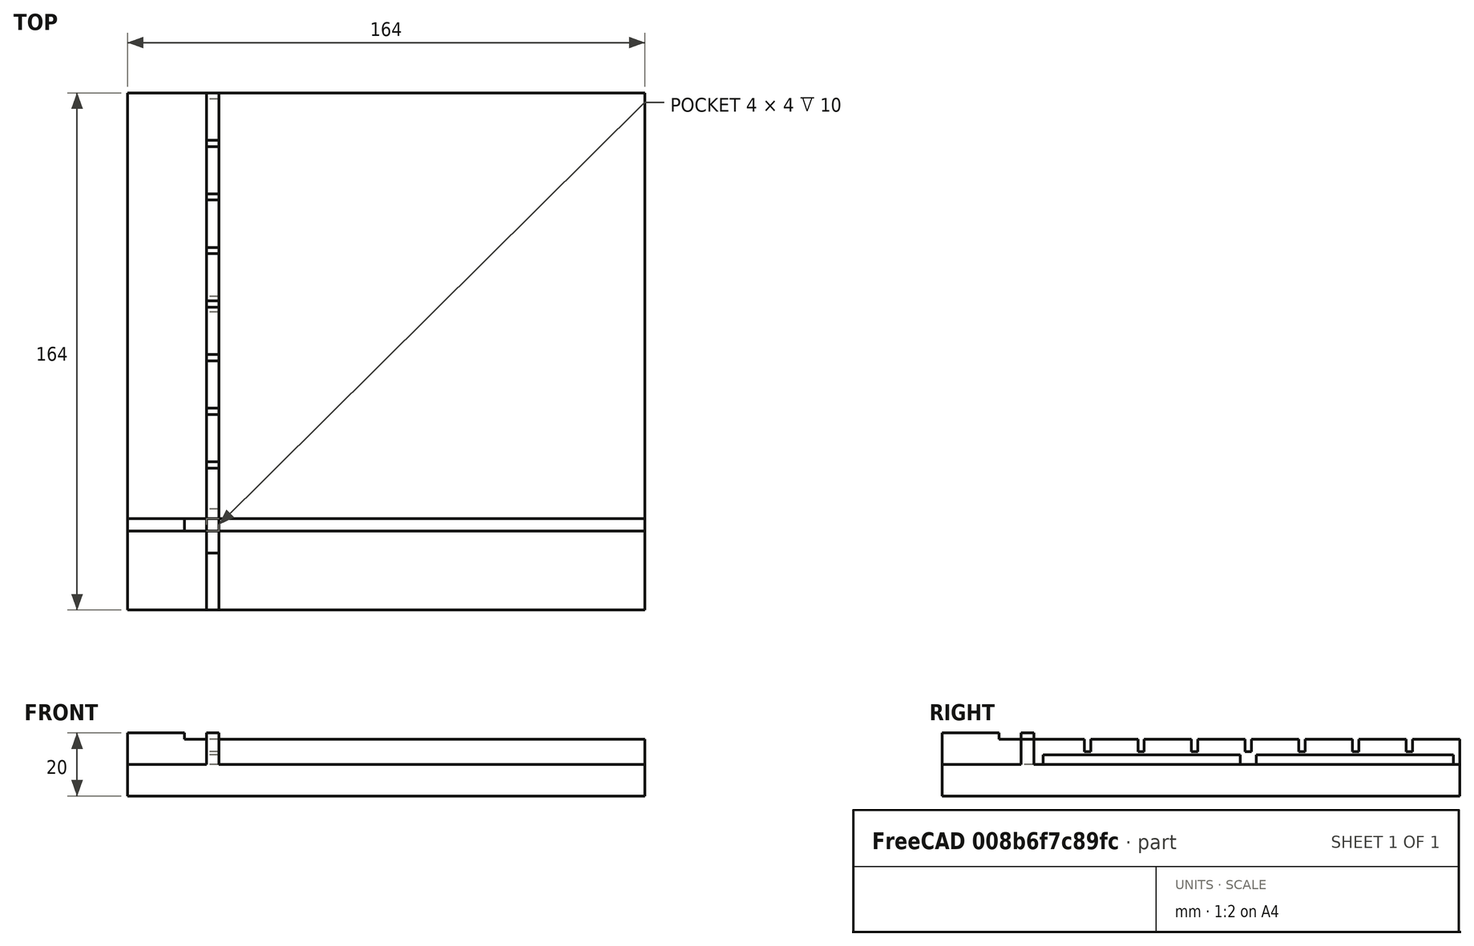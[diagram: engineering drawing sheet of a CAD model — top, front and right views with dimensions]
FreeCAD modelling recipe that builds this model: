
FCSTD DOCUMENT  (FreeCAD 2024.207R38947 (Git))
Label: frame_plate_left_bottom_debugging
License: All rights reserved
LicenseURL: http://en.wikipedia.org/wiki/All_rights_reserved
objects: Sketcher::SketchObject×7, PartDesign::Pocket×4, PartDesign::Pad×2, PartDesign::LinearPattern×1, PartDesign::Body×1
note: 36 computed .brp shape members not serialized (recipe doc carries the construction recipe); baked Part::Feature solids carry a one-line shape summary decoded from their .brp

FEATURE [Sketcher::SketchObject] Sketch  label="LB-plate"
  ArcFitTolerance = 0
  AttachmentSupport = -> [XY_Plane]
  ExternalBSplineMaxDegree = 0
  ExternalBSplineTolerance = 0
  FullyConstrained = true
  InternalTolerance = 1e-06
  InvalidShape = false
  MakeInternals = false
  MapMode = 5
  Support = -> [XY_Plane]
  TreeRank = 0
  ValidateShape = false
  sketch-geometry (4):
    g0: LineSegment StartX=-82 StartY=82 StartZ=0 EndX=82 EndY=82 EndZ=0
    g1: LineSegment StartX=82 StartY=82 StartZ=0 EndX=82 EndY=-82 EndZ=0
    g2: LineSegment StartX=82 StartY=-82 StartZ=0 EndX=-82 EndY=-82 EndZ=0
    g3: LineSegment StartX=-82 StartY=-82 StartZ=0 EndX=-82 EndY=82 EndZ=0
  constraints (10):
    c: Coincident(g0,g1)
    c: Coincident(g1,g2)
    c: Coincident(g2,g3)
    c: Coincident(g3,g0)
    c: Horizontal(g2)
    c: Vertical(g3)
    c: DistanceX(g2,g1) = 164
    c: DistanceY(g2,g0) = 164
    c: Symmetric(g1,g0,g-1)
    c: Symmetric(g0,g0,g-2)
FEATURE [PartDesign::Pad] Pad
  AddSubType = 0
  AutoTaperInnerAngle = true
  CheckUpToFaceLimits = true
  ClaimChildren = false
  Direction = (0,0,1)
  Fit = 0
  FitJoin = 0
  InnerFit = 0
  InnerFitJoin = 0
  InvalidShape = false
  Length = 10
  Length2 = 10
  NewSolid = false
  Profile = -> Sketch
  ReferenceAxis = -> Sketch [N_Axis]
  Suppress = false
  TaperInnerAngle = 0
  TaperInnerAngleRev = 0
  TreeRank = 0
  Type = 0
  ValidateShape = true
  _ProfileBasedVersion = 0
FEATURE [Sketcher::SketchObject] Sketch001  label="LB-bounds"
  ArcFitTolerance = 0
  AttachmentSupport = -> [Pad]
  ExternalBSplineMaxDegree = 0
  ExternalBSplineTolerance = 0
  FullyConstrained = true
  InternalTolerance = 1e-06
  InvalidShape = false
  MakeInternals = false
  MapMode = 5
  Placement = pos=(0,0,10) rot=(0,0,1;0rad)
  Support = -> [Pad]
  TreeRank = 0
  ValidateShape = false
  sketch-geometry (8):
    g0: LineSegment StartX=-82 StartY=-53 StartZ=0 EndX=82 EndY=-53 EndZ=0
    g1: LineSegment StartX=82 StartY=-53 StartZ=0 EndX=82 EndY=-57 EndZ=0
    g2: LineSegment StartX=82 StartY=-57 StartZ=0 EndX=-82 EndY=-57 EndZ=0
    g3: LineSegment StartX=-82 StartY=-57 StartZ=0 EndX=-82 EndY=-53 EndZ=0
    g4: LineSegment StartX=-53 StartY=82 StartZ=0 EndX=-57 EndY=82 EndZ=0
    g5: LineSegment StartX=-57 StartY=82 StartZ=0 EndX=-57 EndY=-82 EndZ=0
    g6: LineSegment StartX=-57 StartY=-82 StartZ=0 EndX=-53 EndY=-82 EndZ=0
    g7: LineSegment StartX=-53 StartY=-82 StartZ=0 EndX=-53 EndY=82 EndZ=0
  constraints (24):
    c: Coincident(g0,g1)
    c: Coincident(g1,g2)
    c: Coincident(g2,g3)
    c: Coincident(g3,g0)
    c: Horizontal(g0)
    c: Horizontal(g2)
    c: Vertical(g1)
    c: Vertical(g3)
    c: DistanceY(g2,g0) = 4
    c: Coincident(g4,g5)
    c: Coincident(g5,g6)
    c: Coincident(g6,g7)
    c: Coincident(g7,g4)
    c: Horizontal(g4)
    c: Horizontal(g6)
    c: Vertical(g5)
    c: Vertical(g7)
    c: DistanceX(g5,g6) = 4
    c: DistanceX(g2,g6) = 29
    c: DistanceY(g5,g0) = 29
    c: DistanceY(g0,g-1) = 53
    c: DistanceX(g6,g-1) = 53
    c: DistanceX(g2,g1) = 164
    c: DistanceY(g5,g4) = 164
FEATURE [PartDesign::Pad] Pad001
  AddSubType = 0
  AutoTaperInnerAngle = true
  BaseFeature = -> Pad
  CheckUpToFaceLimits = true
  ClaimChildren = false
  Direction = (0,0,1)
  Fit = 0
  FitJoin = 0
  InnerFit = 0
  InnerFitJoin = 0
  InvalidShape = false
  Length = 10
  Length2 = 10
  NewSolid = false
  Profile = -> Sketch001
  ReferenceAxis = -> Sketch001 [N_Axis]
  Suppress = false
  TaperInnerAngle = 0
  TaperInnerAngleRev = 0
  TreeRank = 0
  Type = 0
  ValidateShape = true
  _ProfileBasedVersion = 0
FEATURE [Sketcher::SketchObject] Sketch002  label="LB-V-plex-cutout"
  ArcFitTolerance = 0
  AttachmentSupport = -> [Pad001]
  ExternalBSplineMaxDegree = 0
  ExternalBSplineTolerance = 0
  ExternalGeometry = -> [Pad001]
  FullyConstrained = true
  InternalTolerance = 1e-06
  InvalidShape = false
  MakeInternals = false
  MapMode = 5
  Placement = pos=(0,0,10) rot=(0,0,1;0rad)
  Support = -> [Pad001]
  TreeRank = 0
  ValidateShape = false
  sketch-geometry (4):
    g0: LineSegment StartX=-64 StartY=20 StartZ=0 EndX=82 EndY=20 EndZ=0
    g1: LineSegment StartX=82 StartY=20 StartZ=0 EndX=82 EndY=18 EndZ=0
    g2: LineSegment StartX=82 StartY=18 StartZ=0 EndX=-64 EndY=18 EndZ=0
    g3: LineSegment StartX=-64 StartY=18 StartZ=0 EndX=-64 EndY=20 EndZ=0
  constraints (12):
    c: Coincident(g0,g1)
    c: Coincident(g1,g2)
    c: Coincident(g2,g3)
    c: Coincident(g3,g0)
    c: Horizontal(g0)
    c: Horizontal(g2)
    c: Vertical(g1)
    c: Vertical(g3)
    c: PointOnObject(g0,g-3)
    c: DistanceX(g-3,g0) = 18
    c: DistanceY(g2,g0) = 2
    c: PointOnObject(g1,g-4)
FEATURE [PartDesign::Pocket] Pocket
  AddSubType = 1
  AutoTaperInnerAngle = true
  BaseFeature = -> Pad001
  CheckUpToFaceLimits = true
  ClaimChildren = false
  Direction = (-1,0,0)
  Fit = 0
  FitJoin = 0
  InnerFit = 0
  InnerFitJoin = 0
  InvalidShape = false
  Length = 5
  Length2 = 5
  NewSolid = false
  Profile = -> Sketch002
  ReferenceAxis = -> Sketch002 [N_Axis]
  Suppress = false
  TaperInnerAngle = 0
  TaperInnerAngleRev = 0
  TreeRank = 0
  Type = 0
  ValidateShape = true
  _ProfileBasedVersion = 0
  _Version = 0
FEATURE [Sketcher::SketchObject] Sketch003  label="LB-H-grid-cutout"
  ArcFitTolerance = 0
  AttachmentSupport = -> [Pocket]
  ExternalBSplineMaxDegree = 0
  ExternalBSplineTolerance = 0
  ExternalGeometry = -> [Pocket]
  FullyConstrained = true
  InternalTolerance = 1e-06
  InvalidShape = false
  MakeInternals = false
  MapMode = 5
  Placement = pos=(-53,0,0) rot=(0.57735,0.57735,0.57735;2.0944rad)
  Support = -> [Pocket]
  TreeRank = 0
  ValidateShape = false
  sketch-geometry (4):
    g0: LineSegment StartX=-37 StartY=18 StartZ=0 EndX=-35 EndY=18 EndZ=0
    g1: LineSegment StartX=-35 StartY=18 StartZ=0 EndX=-35 EndY=14 EndZ=0
    g2: LineSegment StartX=-35 StartY=14 StartZ=0 EndX=-37 EndY=14 EndZ=0
    g3: LineSegment StartX=-37 StartY=14 StartZ=0 EndX=-37 EndY=18 EndZ=0
  constraints (12):
    c: Coincident(g0,g1)
    c: Coincident(g1,g2)
    c: Coincident(g2,g3)
    c: Coincident(g3,g0)
    c: Horizontal(g0)
    c: Horizontal(g2)
    c: Vertical(g1)
    c: Vertical(g3)
    c: DistanceX(g0,g0) = 2
    c: DistanceY(g1,g0) = 4
    c: PointOnObject(g0,g-4)
    c: DistanceX(g-3,g2) = 16
FEATURE [PartDesign::Pocket] Pocket001
  AddSubType = 1
  AutoTaperInnerAngle = true
  BaseFeature = -> Pocket
  CheckUpToFaceLimits = true
  ClaimChildren = false
  Direction = (-1,0,0)
  Fit = 0
  FitJoin = 0
  InnerFit = 0
  InnerFitJoin = 0
  InvalidShape = false
  Length = 5
  Length2 = 5
  NewSolid = false
  Profile = -> Sketch003
  ReferenceAxis = -> Sketch003 [N_Axis]
  Suppress = false
  TaperInnerAngle = 0
  TaperInnerAngleRev = 0
  TreeRank = 0
  Type = 0
  ValidateShape = true
  _ProfileBasedVersion = 0
  _Version = 0
FEATURE [PartDesign::LinearPattern] LinearPattern
  AddSubType = 0
  BaseFeature = -> Pocket001
  CopyShape = true
  Direction = -> Sketch003 [H_Axis]
  InvalidShape = false
  Length = 136
  NewSolid = false
  Occurrences = 9
  OriginalSubs = -> [Pocket001]
  Originals = -> [Pocket001]
  ParallelTransform = true
  SubTransform = true
  Suppress = false
  TreeRank = 0
  ValidateShape = true
  _Version = 0
FEATURE [Sketcher::SketchObject] Sketch004  label="LB-V-cable-cutout"
  ArcFitTolerance = 0
  AttachmentSupport = -> [YZ_Plane]
  ExternalBSplineMaxDegree = 0
  ExternalBSplineTolerance = 0
  ExternalGeometry = -> [LinearPattern]
  FullyConstrained = true
  InternalTolerance = 1e-06
  InvalidShape = false
  MakeInternals = false
  MapMode = 5
  Placement = pos=(0,0,0) rot=(0.57735,0.57735,0.57735;2.0944rad)
  Support = -> [YZ_Plane]
  TreeRank = 0
  ValidateShape = false
  sketch-geometry (8):
    g0: LineSegment StartX=-50 StartY=13 StartZ=0 EndX=12.5 EndY=13 EndZ=0
    g1: LineSegment StartX=12.5 StartY=13 StartZ=0 EndX=12.5 EndY=10 EndZ=0
    g2: LineSegment StartX=12.5 StartY=10 StartZ=0 EndX=-50 EndY=10 EndZ=0
    g3: LineSegment StartX=-50 StartY=10 StartZ=0 EndX=-50 EndY=13 EndZ=0
    g4: LineSegment StartX=17.5 StartY=13 StartZ=0 EndX=80 EndY=13 EndZ=0
    g5: LineSegment StartX=80 StartY=13 StartZ=0 EndX=80 EndY=10 EndZ=0
    g6: LineSegment StartX=80 StartY=10 StartZ=0 EndX=17.5 EndY=10 EndZ=0
    g7: LineSegment StartX=17.5 StartY=10 StartZ=0 EndX=17.5 EndY=13 EndZ=0
  constraints (24):
    c: Coincident(g0,g1)
    c: Coincident(g1,g2)
    c: Coincident(g2,g3)
    c: Coincident(g3,g0)
    c: Horizontal(g0)
    c: Horizontal(g2)
    c: Vertical(g1)
    c: Vertical(g3)
    c: Coincident(g4,g5)
    c: Coincident(g5,g6)
    c: Coincident(g6,g7)
    c: Coincident(g7,g4)
    c: Horizontal(g4)
    c: Horizontal(g6)
    c: Vertical(g5)
    c: Vertical(g7)
    c: DistanceY(g1,g0) = 3
    c: DistanceY(g6,g4) = 3
    c: DistanceX(g0,g4) = 5
    c: DistanceX(g-3,g0) = 3
    c: PointOnObject(g2,g-4)
    c: PointOnObject(g6,g-4)
    c: DistanceX(g0,g-5) = 1.5
    c: DistanceX(g4,g-6) = 2
FEATURE [PartDesign::Pocket] Pocket002
  AddSubType = 1
  AutoTaperInnerAngle = true
  BaseFeature = -> LinearPattern
  CheckUpToFaceLimits = true
  ClaimChildren = false
  Direction = (-1,2e-16,-3e-16)
  Fit = 0
  FitJoin = 0
  InnerFit = 0
  InnerFitJoin = 0
  InvalidShape = false
  Length = 0
  Length2 = 5
  NewSolid = false
  Offset = 5
  Profile = -> Sketch004
  ReferenceAxis = -> Sketch004 [N_Axis]
  Suppress = false
  TaperInnerAngle = 0
  TaperInnerAngleRev = 0
  TreeRank = 0
  Type = 2
  ValidateShape = true
  _ProfileBasedVersion = 0
  _Version = 0
FEATURE [Sketcher::SketchObject] Sketch005  label="LB-H-plex-cutout"
  ArcFitTolerance = 0
  AttachmentSupport = -> [Pocket002]
  ExternalBSplineMaxDegree = 0
  ExternalBSplineTolerance = 0
  ExternalGeometry = -> [Pocket002]
  FullyConstrained = true
  InternalTolerance = 1e-06
  InvalidShape = false
  MakeInternals = false
  MapMode = 5
  Placement = pos=(0,-53,0) rot=(0,0.707107,0.707107;3.14159rad)
  Support = -> [Pocket002]
  TreeRank = 0
  ValidateShape = false
  sketch-geometry (4):
    g0: LineSegment StartX=-82 StartY=20 StartZ=0 EndX=64 EndY=20 EndZ=0
    g1: LineSegment StartX=64 StartY=20 StartZ=0 EndX=64 EndY=18 EndZ=0
    g2: LineSegment StartX=64 StartY=18 StartZ=0 EndX=-82 EndY=18 EndZ=0
    g3: LineSegment StartX=-82 StartY=18 StartZ=0 EndX=-82 EndY=20 EndZ=0
  constraints (11):
    c: Coincident(g0,g1)
    c: Coincident(g1,g2)
    c: Coincident(g2,g3)
    c: Coincident(g3,g0)
    c: Horizontal(g0)
    c: Horizontal(g2)
    c: Vertical(g1)
    c: Vertical(g3)
    c: Coincident(g-3,g0)
    c: DistanceX(g0,g-4) = 18
    c: DistanceY(g1,g0) = 2
FEATURE [PartDesign::Pocket] Pocket003
  AddSubType = 1
  AutoTaperInnerAngle = true
  BaseFeature = -> Pocket002
  CheckUpToFaceLimits = true
  ClaimChildren = false
  Direction = (0,-1,2e-16)
  Fit = 0
  FitJoin = 0
  InnerFit = 0
  InnerFitJoin = 0
  InvalidShape = false
  Length = 5
  Length2 = 5
  NewSolid = false
  Profile = -> Sketch005
  ReferenceAxis = -> Sketch005 [N_Axis]
  Suppress = false
  TaperInnerAngle = 0
  TaperInnerAngleRev = 0
  TreeRank = 0
  Type = 0
  ValidateShape = true
  _ProfileBasedVersion = 0
  _Version = 0
FEATURE [Sketcher::SketchObject] Sketch007
  ArcFitTolerance = 0
  AttachmentSupport = -> [Pocket003]
  ExternalBSplineMaxDegree = 0
  ExternalBSplineTolerance = 0
  FullyConstrained = false
  InternalTolerance = 1e-06
  InvalidShape = false
  MakeInternals = false
  MapMode = 5
  Placement = pos=(0,82,0) rot=(0,0.707107,0.707107;3.14159rad)
  Support = -> [Pocket003]
  TreeRank = 0
  ValidateShape = false
  sketch-geometry (4):
    g0: LineSegment StartX=-52.1646 StartY=6.35974 StartZ=0 EndX=-35.8444 EndY=6.35974 EndZ=0
    g1: LineSegment StartX=-35.8444 StartY=6.35974 StartZ=0 EndX=-35.8444 EndY=2.32174 EndZ=0
    g2: LineSegment StartX=-35.8444 StartY=2.32174 StartZ=0 EndX=-52.1646 EndY=2.32174 EndZ=0
    g3: LineSegment StartX=-52.1646 StartY=2.32174 StartZ=0 EndX=-52.1646 EndY=6.35974 EndZ=0
  constraints (8):
    c: Coincident(g0,g1)
    c: Coincident(g1,g2)
    c: Coincident(g2,g3)
    c: Coincident(g3,g0)
    c: Horizontal(g0)
    c: Horizontal(g2)
    c: Vertical(g1)
    c: Vertical(g3)
FEATURE [PartDesign::Body] Body  label="LB_plate"
  AutoGroupSolids = false
  ClaimAllChildren = false
  ExportMode = 0
  Group = -> [Sketch,Pad,Sketch001,Pad001,Sketch002,Pocket,Sketch003,Pocket001,LinearPattern,Sketch004,Pocket002,Sketch005,Pocket003,Sketch007]
  InvalidShape = false
  Origin = -> Origin
  Tip = -> Pocket003
  TreeRank = 0
  ValidateShape = false
  _ExportChildren = -> [Pad,Pad001,Pocket,Pocket001,LinearPattern,Pocket002,Pocket003,Sketch007]
  _GroupVersion = 1
